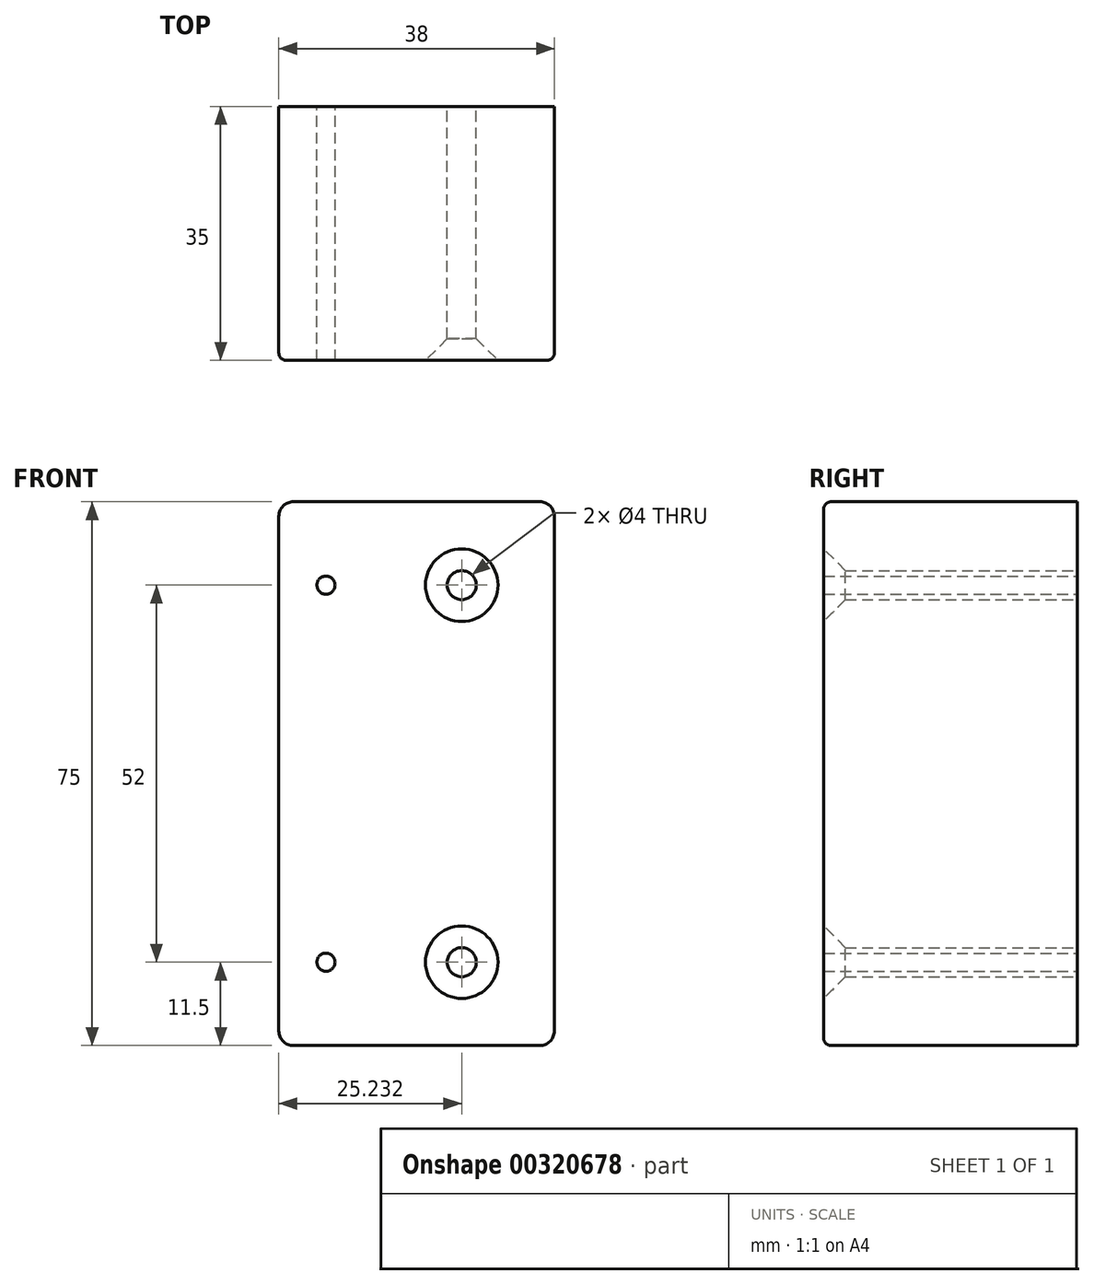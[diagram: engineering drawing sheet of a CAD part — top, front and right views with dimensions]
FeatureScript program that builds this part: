
annotation { "Feature Type Name" : "Feature", "Feature Type Description" : "" }
export const myFeature = defineFeature(function(context is Context, id is Id, definition is map)
    precondition{}
    {
        {
            var Q0;
            Q0=qCreatedBy(makeId("Front.planeOp"),FACE);
            var sketch = newSketch(context, id + "F0", { "sketchPlane" : qUnion([Q0])});
            skLineSegment(sketch, "E0.bottom", {"start": v(19, 37.5) * mm, "end": v(-19, 37.5) * mm});
            skLineSegment(sketch, "E0.top", {"start": v(19, -37.5) * mm, "end": v(-19, -37.5) * mm});
            skLineSegment(sketch, "E0.left", {"start": v(19, 37.5) * mm, "end": v(19, -37.5) * mm});
            skLineSegment(sketch, "E0.right", {"start": v(-19, 37.5) * mm, "end": v(-19, -37.5) * mm});
            skPoint(sketch, "E0.middle", {"position": v(0, 0) * mm});
            skCircle(sketch, "E1", {"center": v(-12.5, 26) * mm, "radius": 1.25 * mm});
            skCircle(sketch, "E2", {"center": v(6.23, 26) * mm, "radius": 2 * mm});
            skCircle(sketch, "E3", {"center": v(6.23, -26) * mm, "radius": 2 * mm});
            skCircle(sketch, "E4", {"center": v(-12.5, -26) * mm, "radius": 1.25 * mm});
            skSolve(sketch);
        }
        {
            var Q0;
            Q0 = qSketchRegion(id + "F0", true);
            extrude(context, id + "F1", {"entities" : qUnion([Q0]), "depth" : 35 * mm});
        }
        {
            var Q0;
            Q0=makeQuery(id+"F1.opExtrude","CAP_EDGE",EDGE,{"disambiguationData":[OSD([sQuery(id+"F0.wireOp",EDGE,"E2")])],"isStart":false});
            var Q1;
            Q1=makeQuery(id+"F1.opExtrude","CAP_EDGE",EDGE,{"disambiguationData":[OSD([sQuery(id+"F0.wireOp",EDGE,"E3")])],"isStart":false});
            chamfer(context, id + "F2", {"entities" : qUnion([Q0, Q1]), "chamferType" : ChamferType.OFFSET_ANGLE, "width" : 3 * mm, "oppositeDirection" : false, "angle" : 45 * degree, "tangentPropagation" : true});
        }
        {
            var Q0;
            Q0=makeQuery(id+"F1.opExtrude","SWEPT_EDGE",EDGE,{"disambiguationData":[OSD([sQuery(id+"F0.wireOp",EDGE,"E0.bottom"),sQuery(id+"F0.wireOp",EDGE,"E0.right")])]});
            var Q1;
            Q1=makeQuery(id+"F1.opExtrude","SWEPT_EDGE",EDGE,{"disambiguationData":[OSD([sQuery(id+"F0.wireOp",EDGE,"E0.top"),sQuery(id+"F0.wireOp",EDGE,"E0.right")])]});
            var Q2;
            Q2=makeQuery(id+"F1.opExtrude","SWEPT_EDGE",EDGE,{"disambiguationData":[OSD([sQuery(id+"F0.wireOp",EDGE,"E0.top"),sQuery(id+"F0.wireOp",EDGE,"E0.left")])]});
            var Q3;
            Q3=makeQuery(id+"F1.opExtrude","SWEPT_EDGE",EDGE,{"disambiguationData":[OSD([sQuery(id+"F0.wireOp",EDGE,"E0.bottom"),sQuery(id+"F0.wireOp",EDGE,"E0.left")])]});
            fillet(context, id + "F3", {"entities" : qUnion([Q0, Q1, Q2, Q3]), "radius" : 2 * mm, "tangentPropagation" : true, "allowEdgeOverflow" : false});
        }
        {
            var Q0;
            Q0=makeQuery(id+"F1.opExtrude","CAP_EDGE",EDGE,{"disambiguationData":[OSD([sQuery(id+"F0.wireOp",EDGE,"E0.right")])],"isStart":false});
            fillet(context, id + "F4", {"entities" : qUnion([Q0]), "radius" : 1 * mm, "tangentPropagation" : true, "allowEdgeOverflow" : false});
        }
    });
